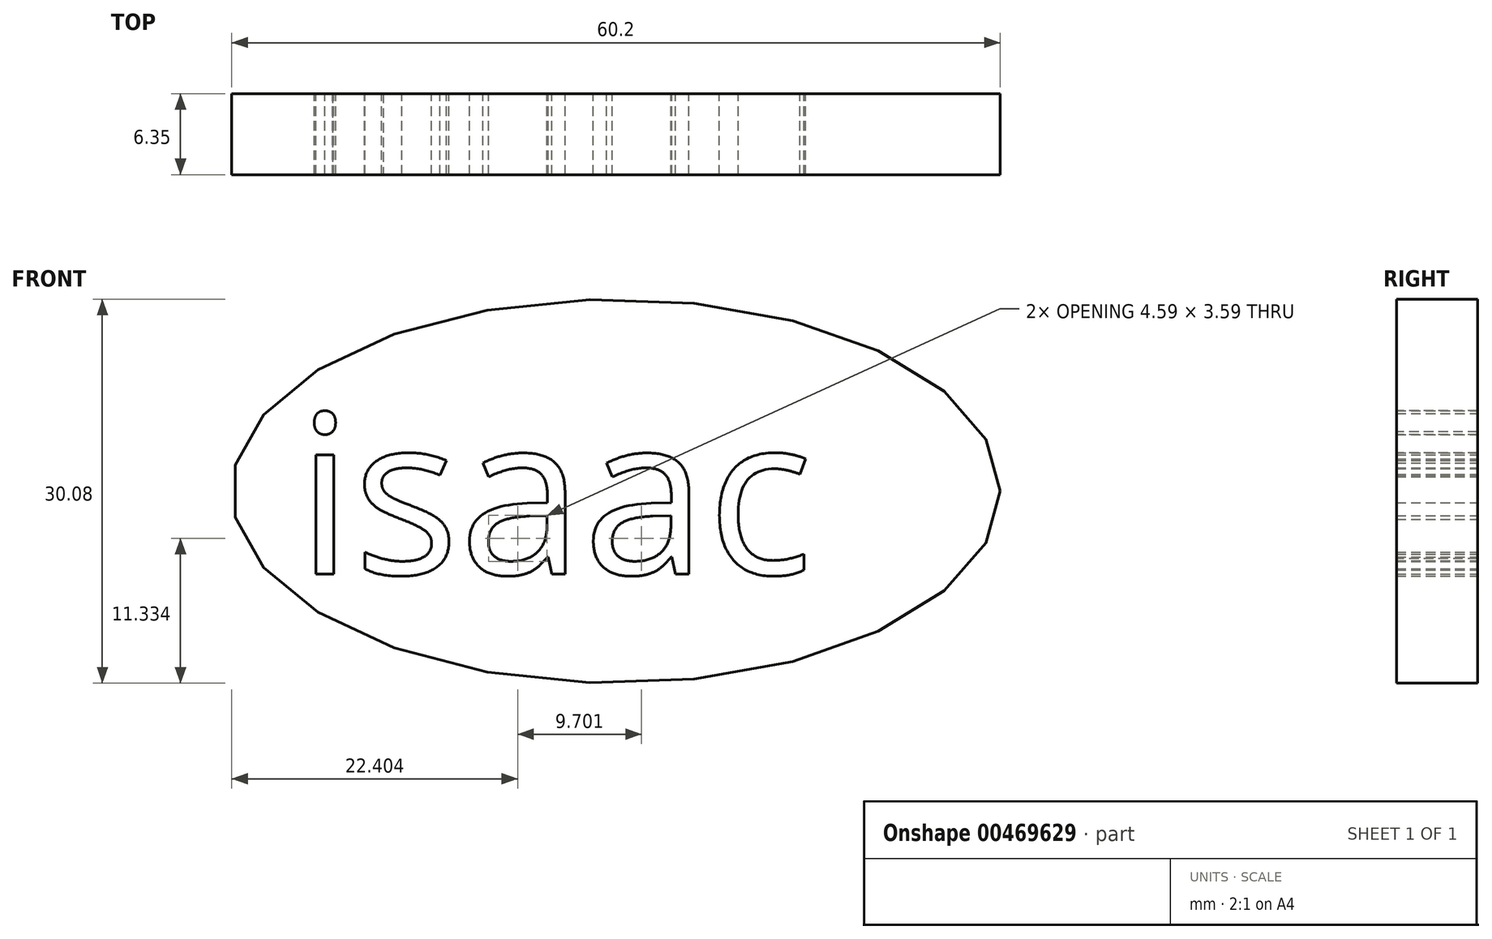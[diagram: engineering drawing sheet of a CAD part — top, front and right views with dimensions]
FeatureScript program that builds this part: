
annotation { "Feature Type Name" : "Feature", "Feature Type Description" : "" }
export const myFeature = defineFeature(function(context is Context, id is Id, definition is map)
    precondition{}
    {
        {
            var Q0;
            Q0=qCreatedBy(makeId("Front.planeOp"),FACE);
            var sketch = newSketch(context, id + "F0", { "sketchPlane" : qUnion([Q0])});
            skEllipse(sketch, "E0", {"center": v(0, 0) * mm, "majorRadius": 30.1 * mm, "minorRadius": 15.04 * mm, "majorAxis": v(1, 0)});
            skSolve(sketch);
        }
        {
            var Q0;
            Q0=qCreatedBy(makeId("Front.planeOp"),FACE);
            var sketch = newSketch(context, id + "F1", { "sketchPlane" : qUnion([Q0])});
            skText(sketch, "E1", { "text": "isaac", "fontName": "OpenSans-Regular.ttf"});
            const initialGuessF1  = {"E1": [-0.02501, -0.0065, 1, 0, 0.01256]};
            skSetInitialGuess(sketch, initialGuessF1);
            skSolve(sketch);
        }
        {
            var Q0;
            Q0 = qSketchRegion(id + "F1", true);
            var Q1;
            Q1=makeQuery(id+"F0.imprint","IMPRINT",FACE,{"disambiguationData":[TD([[makeQuery(id+"F0.imprint","IMPRINT",EDGE,{"derivedFrom":sQuery(id+"F0.wireOp",EDGE,"E0")}),1.0]])]});
            extrude(context, id + "F2", {"entities" : qUnion([Q0, Q1]), "depth" : 6.35 * mm});
        }
        {
            var Q0;
            Q0 = qSketchRegion(id + "F1", true);
            extrude(context, id + "F3", {"entities" : qUnion([Q0]), "operationType" : NewBodyOperationType.REMOVE, "oppositeDirection" : true, "depth" : 3.17 * mm});
        }
    });
